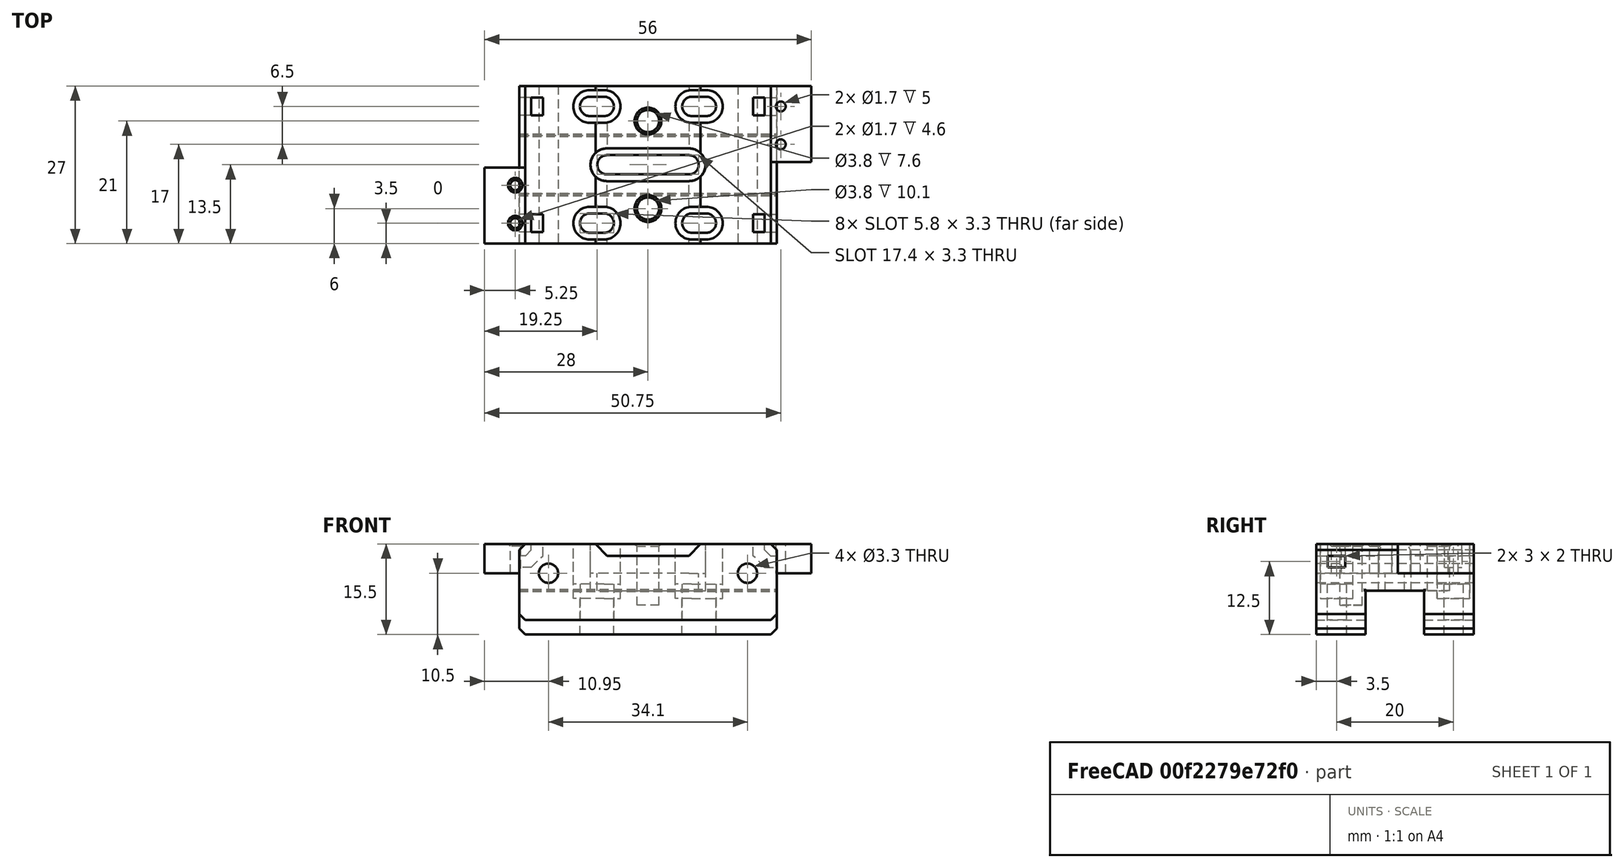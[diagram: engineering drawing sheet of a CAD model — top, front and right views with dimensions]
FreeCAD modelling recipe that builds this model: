
FCSTD DOCUMENT  (FreeCAD 0.19R24291 (Git))
Label: top-plate-with-endstop
License: All rights reserved
LicenseURL: http://en.wikipedia.org/wiki/All_rights_reserved
objects: Part::Feature×2, PartDesign::Pocket×2, PartDesign::FeatureBase×1, PartDesign::Pad×1, PartDesign::Chamfer×1, PartDesign::Body×1
note: 12 computed .brp shape members not serialized (recipe doc carries the construction recipe); baked Part::Feature solids carry a one-line shape summary decoded from their .brp

FEATURE [Part::Feature] Body001002001  label="top-plate-with-endstop-2020"
  Placement = pos=(0,0,0) rot=(0,0,1;3.14159rad)
  shape: bbox 50.05 x 27 x 13 mm, 100 faces (baked)
FEATURE [Part::Feature] Body001002002  label="top-plate-with-endstop-base"
  Placement = pos=(0,0,0) rot=(0,0,1;3.14159rad)
  shape: bbox 50.05 x 27 x 13 mm, 100 faces (baked)
FEATURE [PartDesign::FeatureBase] BaseFeature
  BaseFeature = -> Body001002002
FEATURE [PartDesign::Pad] Pad
  BaseFeature = -> BaseFeature
  Direction = (1,1,1)
  Length = 2.5
  Length2 = 100
  Profile = -> BaseFeature [Face17,Face55,Face14,Face36,Face54,Face47]
  Reversed = true
  Type = 0
FEATURE [PartDesign::Pocket] Pocket
  BaseFeature = -> Pad
  Length = 2.5
  Length2 = 100
  Profile = -> Pad [Face71,Face66,Face70,Face72,Face68,Face116]
  Type = 0
FEATURE [PartDesign::Chamfer] Chamfer
  Angle = 45
  Base = -> Pocket [Edge42,Edge43]
  BaseFeature = -> Pocket
  ChamferType = 0
  FlipDirection = false
  Refine = true
  Size = 0.4
  Size2 = 1
  SupportTransform = false
FEATURE [PartDesign::Pocket] Pocket001
  BaseFeature = -> Chamfer
  Length = 5
  Length2 = 100
  Profile = -> Chamfer [Face11]
  Refine = true
  Type = 0
FEATURE [PartDesign::Body] Body  label="top-plate-with-endstop-1515"
  BaseFeature = -> Body001002002
  Group = -> [BaseFeature,Pad,Pocket,Chamfer,Pocket001]
  Origin = -> Origin
  Tip = -> Pocket001
